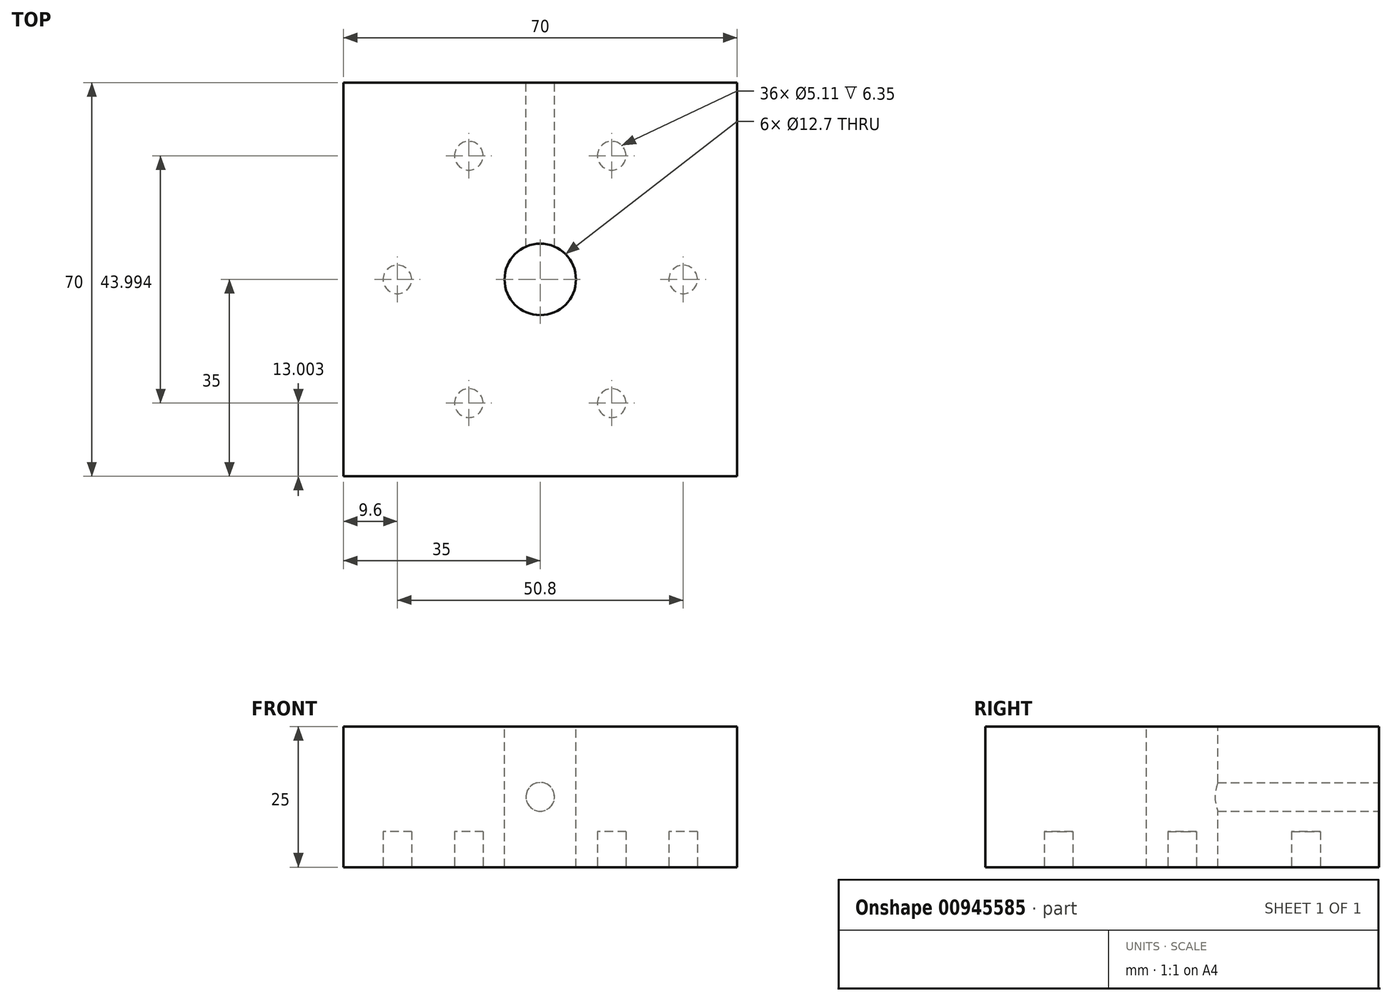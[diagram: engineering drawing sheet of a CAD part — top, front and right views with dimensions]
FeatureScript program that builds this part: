
annotation { "Feature Type Name" : "Feature", "Feature Type Description" : "" }
export const myFeature = defineFeature(function(context is Context, id is Id, definition is map)
    precondition{}
    {
        {
            var Q0;
            Q0=qCreatedBy(makeId("Top.planeOp"),FACE);
            var sketch = newSketch(context, id + "F0", { "sketchPlane" : qUnion([Q0])});
            skLineSegment(sketch, "E0.bottom", {"start": v(35, 35) * mm, "end": v(-35, 35) * mm});
            skLineSegment(sketch, "E0.top", {"start": v(35, -35) * mm, "end": v(-35, -35) * mm});
            skLineSegment(sketch, "E0.left", {"start": v(35, 35) * mm, "end": v(35, -35) * mm});
            skLineSegment(sketch, "E0.right", {"start": v(-35, 35) * mm, "end": v(-35, -35) * mm});
            skPoint(sketch, "E0.middle", {"position": v(0, 0) * mm});
            skSolve(sketch);
        }
        {
            var Q0;
            Q0=qSketchRegion(id+"F0",true);
            extrude(context, id + "F1", {"entities" : qUnion([Q0]), "depth" : 25 * mm, "offsetDistance" : 25 * mm});
        }
        {
            var Q0;
            Q0=qCreatedBy(makeId("Top.planeOp"),FACE);
            var sketch = newSketch(context, id + "F2", { "sketchPlane" : qUnion([Q0])});
            skCircle(sketch, "E1", {"center": v(0, 0) * mm, "radius": 2.55 * mm});
            skCircle(sketch, "E2.cCircle", {"center": v(0, 0) * mm, "radius": 25.4 * mm, "construction": true});
            skLineSegment(sketch, "E2.0", {"start": v(25.4, 0) * mm, "end": v(12.7, -22) * mm, "construction": true});
            skLineSegment(sketch, "E2.1", {"start": v(12.7, -22) * mm, "end": v(-12.7, -22) * mm, "construction": true});
            skLineSegment(sketch, "E2.2", {"start": v(-12.7, -22) * mm, "end": v(-25.4, 0) * mm, "construction": true});
            skLineSegment(sketch, "E2.3", {"start": v(-25.4, 0) * mm, "end": v(-12.7, 22) * mm, "construction": true});
            skLineSegment(sketch, "E2.4", {"start": v(-12.7, 22) * mm, "end": v(12.7, 22) * mm, "construction": true});
            skLineSegment(sketch, "E2.5", {"start": v(12.7, 22) * mm, "end": v(25.4, 0) * mm, "construction": true});
            skCircle(sketch, "E3", {"center": v(-25.4, 0) * mm, "radius": 2.55 * mm});
            skCircle(sketch, "E4.1.0", {"center": v(-12.7, -22) * mm, "radius": 2.55 * mm});
            skCircle(sketch, "E4.2.0", {"center": v(12.7, -22) * mm, "radius": 2.55 * mm});
            skCircle(sketch, "E4.3.0", {"center": v(25.4, 0) * mm, "radius": 2.55 * mm});
            skCircle(sketch, "E4.4.0", {"center": v(12.7, 22) * mm, "radius": 2.55 * mm});
            skCircle(sketch, "E4.5.0", {"center": v(-12.7, 22) * mm, "radius": 2.55 * mm});
            skSolve(sketch);
        }
        {
            var Q0;
            Q0=qSketchRegion(id+"F2",true);
            extrude(context, id + "F3", {"entities" : qUnion([Q0]), "operationType" : NewBodyOperationType.REMOVE, "depth" : 6.35 * mm, "offsetDistance" : 25 * mm});
        }
        {
            var Q0;
            Q0=makeQuery(id+"F1.opExtrude","CAP_FACE",FACE,{"disambiguationData":[OSD([sQuery(id+"F0.wireOp",EDGE,"E0.bottom"),sQuery(id+"F0.wireOp",EDGE,"E0.top"),sQuery(id+"F0.wireOp",EDGE,"E0.left"),sQuery(id+"F0.wireOp",EDGE,"E0.right")])],"isStart":false});
            var sketch = newSketch(context, id + "F4", { "sketchPlane" : qUnion([Q0])});
            skCircle(sketch, "E5", {"center": v(0, 0) * mm, "radius": 6.35 * mm});
            skSolve(sketch);
        }
        {
            var Q0;
            Q0=qSketchRegion(id+"F4",true);
            var Q1;
            Q1=makeQuery(id+"F1.opExtrude","CAP_FACE",FACE,{"disambiguationData":[OSD([sQuery(id+"F0.wireOp",EDGE,"E0.bottom"),sQuery(id+"F0.wireOp",EDGE,"E0.top"),sQuery(id+"F0.wireOp",EDGE,"E0.left"),sQuery(id+"F0.wireOp",EDGE,"E0.right")])],"isStart":true});
            extrude(context, id + "F5", {"entities" : qUnion([Q0]), "operationType" : NewBodyOperationType.REMOVE, "endBound" : BoundingType.UP_TO_SURFACE, "oppositeDirection" : true, "depth" : 25 * mm, "endBoundEntityFace" : qUnion([Q1]), "offsetDistance" : 25 * mm});
        }
        {
            var Q0;
            Q0=makeQuery(id+"F1.opExtrude","SWEPT_FACE",FACE,{"disambiguationData":[OSD([sQuery(id+"F0.wireOp",EDGE,"E0.bottom")])]});
            var sketch = newSketch(context, id + "F6", { "sketchPlane" : qUnion([Q0])});
            skCircle(sketch, "E6", {"center": v(0, 12.5) * mm, "radius": 2.55 * mm});
            skLineSegment(sketch, "E7", {"start": v(0, 0) * mm, "end": v(0, 25) * mm, "construction": true});
            skSolve(sketch);
        }
        {
            var Q0;
            Q0 = qSketchRegion(id + "F6", true);
            var Q1;
            Q1=makeQuery(id+"F5.boolean.opBoolean","COPY",FACE,{"derivedFrom":makeQuery(id+"F5.opExtrude","SWEPT_FACE",FACE,{"disambiguationData":[OSD([sQuery(id+"F4.wireOp",EDGE,"E5")])]})});
            extrude(context, id + "F7", {"entities" : qUnion([Q0]), "operationType" : NewBodyOperationType.REMOVE, "endBound" : BoundingType.UP_TO_SURFACE, "oppositeDirection" : true, "depth" : 25 * mm, "endBoundEntityFace" : qUnion([Q1]), "offsetDistance" : 25 * mm});
        }
    });
